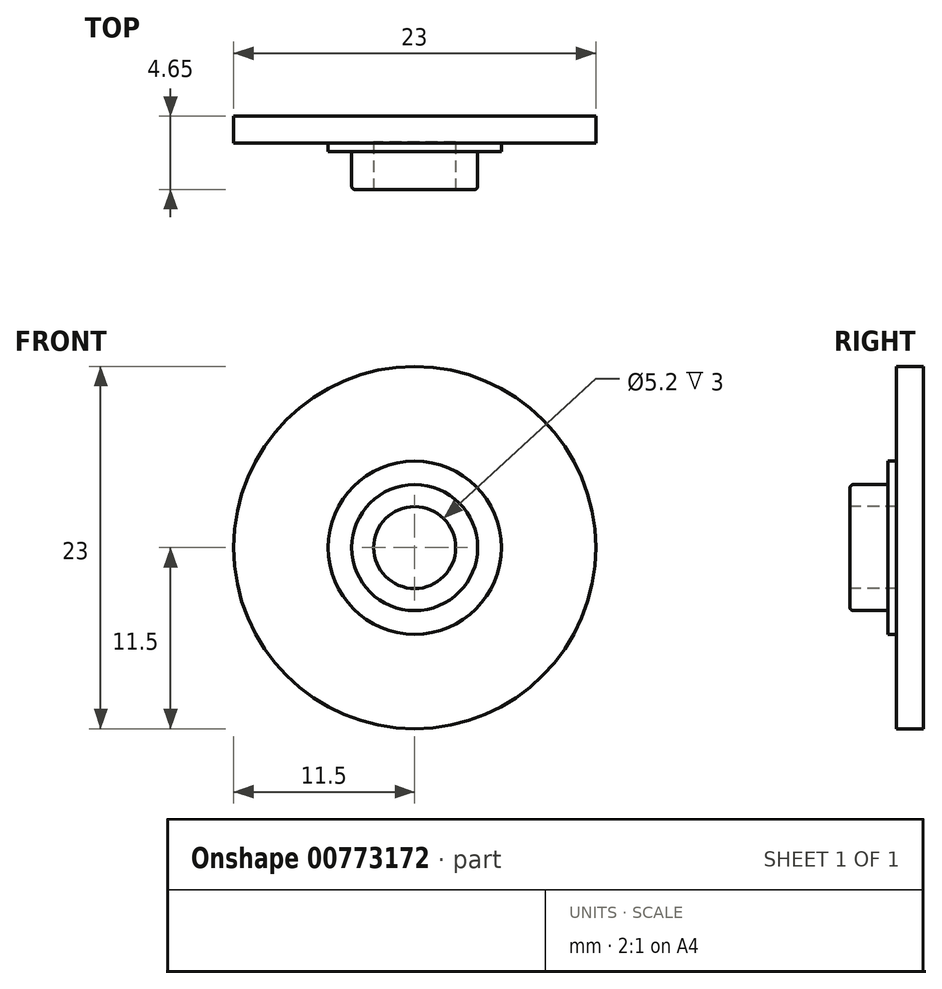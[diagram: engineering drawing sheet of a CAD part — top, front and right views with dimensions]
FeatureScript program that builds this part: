
annotation { "Feature Type Name" : "Feature", "Feature Type Description" : "" }
export const myFeature = defineFeature(function(context is Context, id is Id, definition is map)
    precondition{}
    {
        {
            var Q0;
            Q0=qCreatedBy(makeId("Front.planeOp"),FACE);
            var sketch = newSketch(context, id + "F0", { "sketchPlane" : qUnion([Q0])});
            skCircle(sketch, "E0", {"center": v(0, 0) * mm, "radius": 11.5 * mm});
            skSolve(sketch);
        }
        {
            var Q0;
            Q0=makeQuery(id+"F0.imprint","IMPRINT",FACE,{"disambiguationData":[TD([[makeQuery(id+"F0.imprint","IMPRINT",EDGE,{"derivedFrom":sQuery(id+"F0.wireOp",EDGE,"E0")}),1.0]])]});
            extrude(context, id + "F1", {"entities" : qUnion([Q0]), "depth" : 1.7 * mm, "offsetDistance" : 25 * mm});
        }
        {
            var Q0;
            Q0=qCreatedBy(makeId("Front.planeOp"),FACE);
            var sketch = newSketch(context, id + "F2", { "sketchPlane" : qUnion([Q0])});
            skCircle(sketch, "E1", {"center": v(0, 0) * mm, "radius": 5.5 * mm});
            skSolve(sketch);
        }
        {
            var Q0;
            Q0 = qSketchRegion(id + "F2", true);
            extrude(context, id + "F3", {"entities" : qUnion([Q0]), "operationType" : NewBodyOperationType.ADD, "depth" : 2.25 * mm, "offsetDistance" : 25 * mm});
        }
        {
            var Q0;
            Q0=qCreatedBy(makeId("Front.planeOp"),FACE);
            var sketch = newSketch(context, id + "F4", { "sketchPlane" : qUnion([Q0])});
            skCircle(sketch, "E2", {"center": v(0, 0) * mm, "radius": 4 * mm});
            skSolve(sketch);
        }
        {
            var Q0;
            Q0=makeQuery(id+"F4.imprint","IMPRINT",FACE,{"disambiguationData":[TD([[makeQuery(id+"F4.imprint","IMPRINT",EDGE,{"derivedFrom":sQuery(id+"F4.wireOp",EDGE,"E2")}),1.0]])]});
            extrude(context, id + "F5", {"entities" : qUnion([Q0]), "operationType" : NewBodyOperationType.ADD, "depth" : 4.65 * mm, "offsetDistance" : 25 * mm});
        }
        {
            var Q0;
            Q0=makeQuery(id+"F5.opExtrude","CAP_EDGE",EDGE,{"disambiguationData":[OSD([sQuery(id+"F4.wireOp",EDGE,"E2")])],"isStart":false});
            fillet(context, id + "F6", {"entities" : qUnion([Q0]), "radius" : 0.2 * mm, "tangentPropagation" : true, "allowEdgeOverflow" : false});
        }
        {
            var Q0;
            Q0=makeQuery(id+"F5.opExtrude","CAP_FACE",FACE,{"disambiguationData":[OSD([sQuery(id+"F4.wireOp",EDGE,"E2")])],"isStart":false});
            var sketch = newSketch(context, id + "F7", { "sketchPlane" : qUnion([Q0])});
            skCircle(sketch, "E3", {"center": v(0, 0) * mm, "radius": 2.6 * mm});
            skSolve(sketch);
        }
        {
            var Q0;
            Q0=makeQuery(id+"F7.imprint","IMPRINT",FACE,{"disambiguationData":[TD([[makeQuery(id+"F7.imprint","IMPRINT",EDGE,{"derivedFrom":sQuery(id+"F7.wireOp",EDGE,"E3")}),1.0]])]});
            extrude(context, id + "F8", {"entities" : qUnion([Q0]), "operationType" : NewBodyOperationType.REMOVE, "oppositeDirection" : true, "depth" : 3 * mm, "offsetDistance" : 25 * mm});
        }
    });
